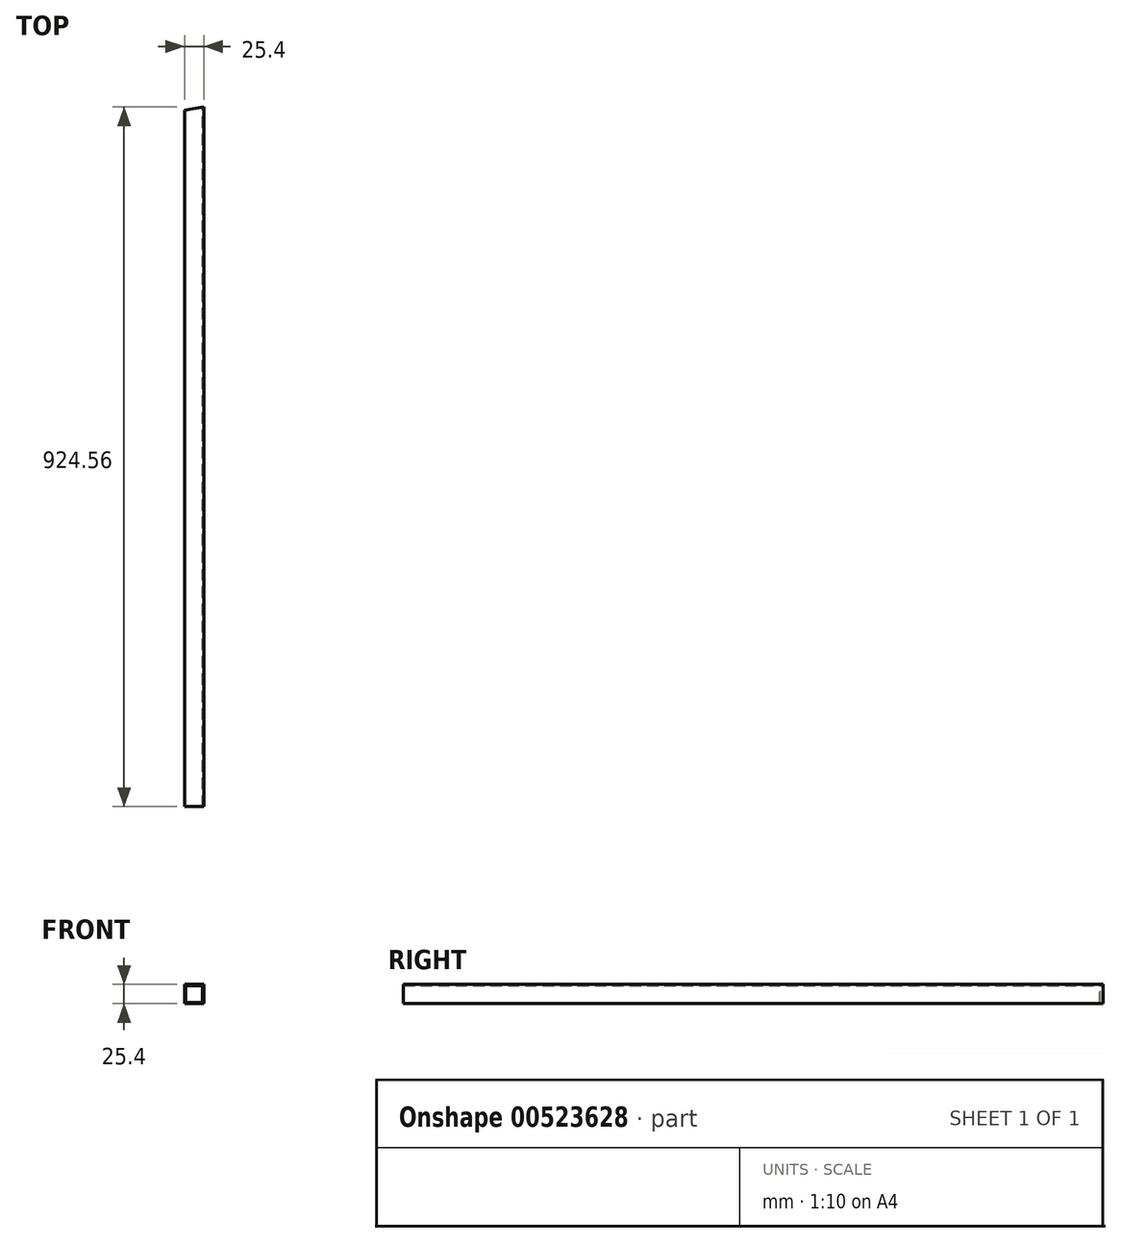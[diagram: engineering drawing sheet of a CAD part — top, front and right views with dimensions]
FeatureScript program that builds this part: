
annotation { "Feature Type Name" : "Feature", "Feature Type Description" : "" }
export const myFeature = defineFeature(function(context is Context, id is Id, definition is map)
    precondition{}
    {
        {
            var Q0;
            Q0=qCreatedBy(makeId("Front.planeOp"),FACE);
            var sketch = newSketch(context, id + "F0", { "sketchPlane" : qUnion([Q0])});
            skLineSegment(sketch, "E0.bottom", {"start": v(-12.7, -12.7) * mm, "end": v(12.7, -12.7) * mm});
            skLineSegment(sketch, "E0.top", {"start": v(-12.7, 12.7) * mm, "end": v(12.7, 12.7) * mm});
            skLineSegment(sketch, "E0.left", {"start": v(-12.7, -12.7) * mm, "end": v(-12.7, 12.7) * mm});
            skLineSegment(sketch, "E0.right", {"start": v(12.7, -12.7) * mm, "end": v(12.7, 12.7) * mm});
            skLineSegment(sketch, "E1.bottom", {"start": v(-11.11, -11.11) * mm, "end": v(11.11, -11.11) * mm});
            skLineSegment(sketch, "E1.top", {"start": v(-11.11, 11.11) * mm, "end": v(11.11, 11.11) * mm});
            skLineSegment(sketch, "E1.left", {"start": v(-11.11, -11.11) * mm, "end": v(-11.11, 11.11) * mm});
            skLineSegment(sketch, "E1.right", {"start": v(11.11, -11.11) * mm, "end": v(11.11, 11.11) * mm});
            skLineSegment(sketch, "E2", {"start": v(-11.11, 0) * mm, "end": v(11.11, 0) * mm, "construction": true});
            skLineSegment(sketch, "E3", {"start": v(0, 12.7) * mm, "end": v(0, -12.7) * mm, "construction": true});
            skSolve(sketch);
        }
        {
            var Q0;
            Q0=qSketchRegion(id+"F0",true);
            extrude(context, id + "F1", {"entities" : qUnion([Q0]), "endBound" : BoundingType.SYMMETRIC, "depth" : 924.56 * mm, "offsetDistance" : 25.4 * mm});
        }
        {
            var Q0;
            Q0=makeQuery(id+"F1.opExtrude","SWEPT_FACE",FACE,{"disambiguationData":[OSD([sQuery(id+"F0.wireOp",EDGE,"E0.top")])]});
            var sketch = newSketch(context, id + "F2", { "sketchPlane" : qUnion([Q0])});
            skLineSegment(sketch, "E4", {"start": v(-12.7, 462.28) * mm, "end": v(-12.7, 457.8) * mm});
            skLineSegment(sketch, "E5", {"start": v(-12.7, 457.8) * mm, "end": v(12.7, 462.28) * mm});
            skLineSegment(sketch, "E6", {"start": v(12.7, 462.28) * mm, "end": v(-12.7, 462.28) * mm});
            skSolve(sketch);
        }
        {
            var Q0;
            Q0=qSketchRegion(id+"F2",true);
            extrude(context, id + "F3", {"entities" : qUnion([Q0]), "operationType" : NewBodyOperationType.REMOVE, "endBound" : BoundingType.THROUGH_ALL, "oppositeDirection" : true, "depth" : 25.4 * mm, "offsetDistance" : 25.4 * mm});
        }
    });
